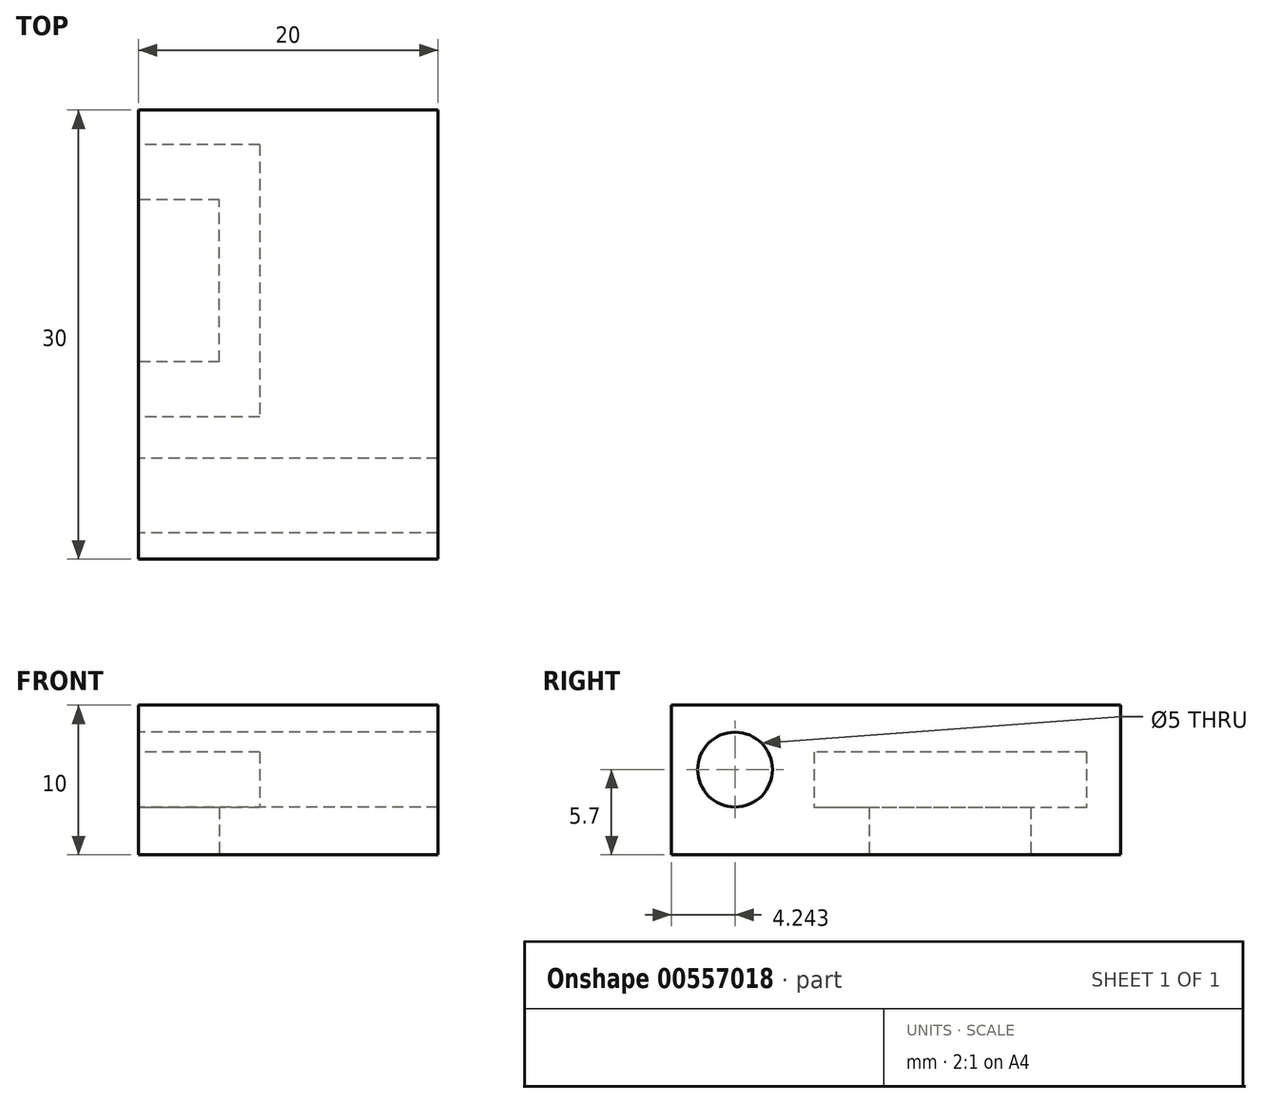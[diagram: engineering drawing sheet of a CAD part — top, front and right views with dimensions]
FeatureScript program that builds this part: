
annotation { "Feature Type Name" : "Feature", "Feature Type Description" : "" }
export const myFeature = defineFeature(function(context is Context, id is Id, definition is map)
    precondition{}
    {
        {
            var Q0;
            Q0=qCreatedBy(makeId("Top.planeOp"),FACE);
            var sketch = newSketch(context, id + "F0", { "sketchPlane" : qUnion([Q0])});
            skLineSegment(sketch, "E0.bottom", {"start": v(10, -15) * mm, "end": v(-10, -15) * mm});
            skLineSegment(sketch, "E0.top", {"start": v(10, 15) * mm, "end": v(-10, 15) * mm});
            skLineSegment(sketch, "E0.left", {"start": v(10, -15) * mm, "end": v(10, 15) * mm});
            skLineSegment(sketch, "E0.right", {"start": v(-10, -15) * mm, "end": v(-10, 15) * mm});
            skPoint(sketch, "E0.middle", {"position": v(0, 0) * mm});
            skSolve(sketch);
        }
        {
            var Q0;
            Q0=qSketchRegion(id+"F0",true);
            extrude(context, id + "F1", {"entities" : qUnion([Q0]), "depth" : 10 * mm, "offsetDistance" : 25 * mm});
        }
        {
            var Q0;
            Q0=makeQuery(id+"F1.opExtrude","SWEPT_FACE",FACE,{"disambiguationData":[OSD([sQuery(id+"F0.wireOp",EDGE,"E0.right")])]});
            var sketch = newSketch(context, id + "F2", { "sketchPlane" : qUnion([Q0])});
            skLineSegment(sketch, "E1.bottom", {"start": v(-9, 3.16) * mm, "end": v(1.8, 3.16) * mm});
            skLineSegment(sketch, "E1.top", {"start": v(-9, 0) * mm, "end": v(1.8, 0) * mm});
            skLineSegment(sketch, "E1.left", {"start": v(-9, 3.16) * mm, "end": v(-9, 0) * mm});
            skLineSegment(sketch, "E1.right", {"start": v(1.8, 3.16) * mm, "end": v(1.8, 0) * mm});
            skLineSegment(sketch, "E2.bottom", {"start": v(-12.7, 6.87) * mm, "end": v(5.5, 6.87) * mm});
            skLineSegment(sketch, "E2.top", {"start": v(-12.7, 3.16) * mm, "end": v(5.5, 3.16) * mm});
            skLineSegment(sketch, "E2.left", {"start": v(-12.7, 6.87) * mm, "end": v(-12.7, 3.16) * mm});
            skLineSegment(sketch, "E2.right", {"start": v(5.5, 6.87) * mm, "end": v(5.5, 3.16) * mm});
            skSolve(sketch);
        }
        {
            var Q0;
            Q0=makeQuery(id+"F2.imprint","IMPRINT",FACE,{"disambiguationData":[TD([[makeQuery(id+"F2.imprint","IMPRINT",EDGE,{"derivedFrom":sQuery(id+"F2.wireOp",EDGE,"E1.top")}),-1.0]])]});
            extrude(context, id + "F3", {"entities" : qUnion([Q0]), "operationType" : NewBodyOperationType.REMOVE, "oppositeDirection" : true, "depth" : 5.4 * mm, "offsetDistance" : 25 * mm});
        }
        {
            var Q0;
            Q0=makeQuery(id+"F2.imprint","IMPRINT",FACE,{"disambiguationData":[TD([[makeQuery(id+"F2.imprint","IMPRINT",EDGE,{"derivedFrom":sQuery(id+"F2.wireOp",EDGE,"E2.bottom")}),-1.0]])]});
            extrude(context, id + "F4", {"entities" : qUnion([Q0]), "operationType" : NewBodyOperationType.REMOVE, "oppositeDirection" : true, "depth" : 8.1 * mm, "offsetDistance" : 25 * mm});
        }
        {
            var Q0;
            Q0=makeQuery(id+"F1.opExtrude","SWEPT_FACE",FACE,{"disambiguationData":[OSD([sQuery(id+"F0.wireOp",EDGE,"E0.right")])]});
            var sketch = newSketch(context, id + "F5", { "sketchPlane" : qUnion([Q0])});
            skCircle(sketch, "E3", {"center": v(10.76, 5.7) * mm, "radius": 2.5 * mm});
            skSolve(sketch);
        }
        {
            var Q0;
            Q0=qSketchRegion(id+"F5",true);
            extrude(context, id + "F6", {"entities" : qUnion([Q0]), "operationType" : NewBodyOperationType.REMOVE, "oppositeDirection" : true, "depth" : 20 * mm, "offsetDistance" : 25 * mm});
        }
    });
